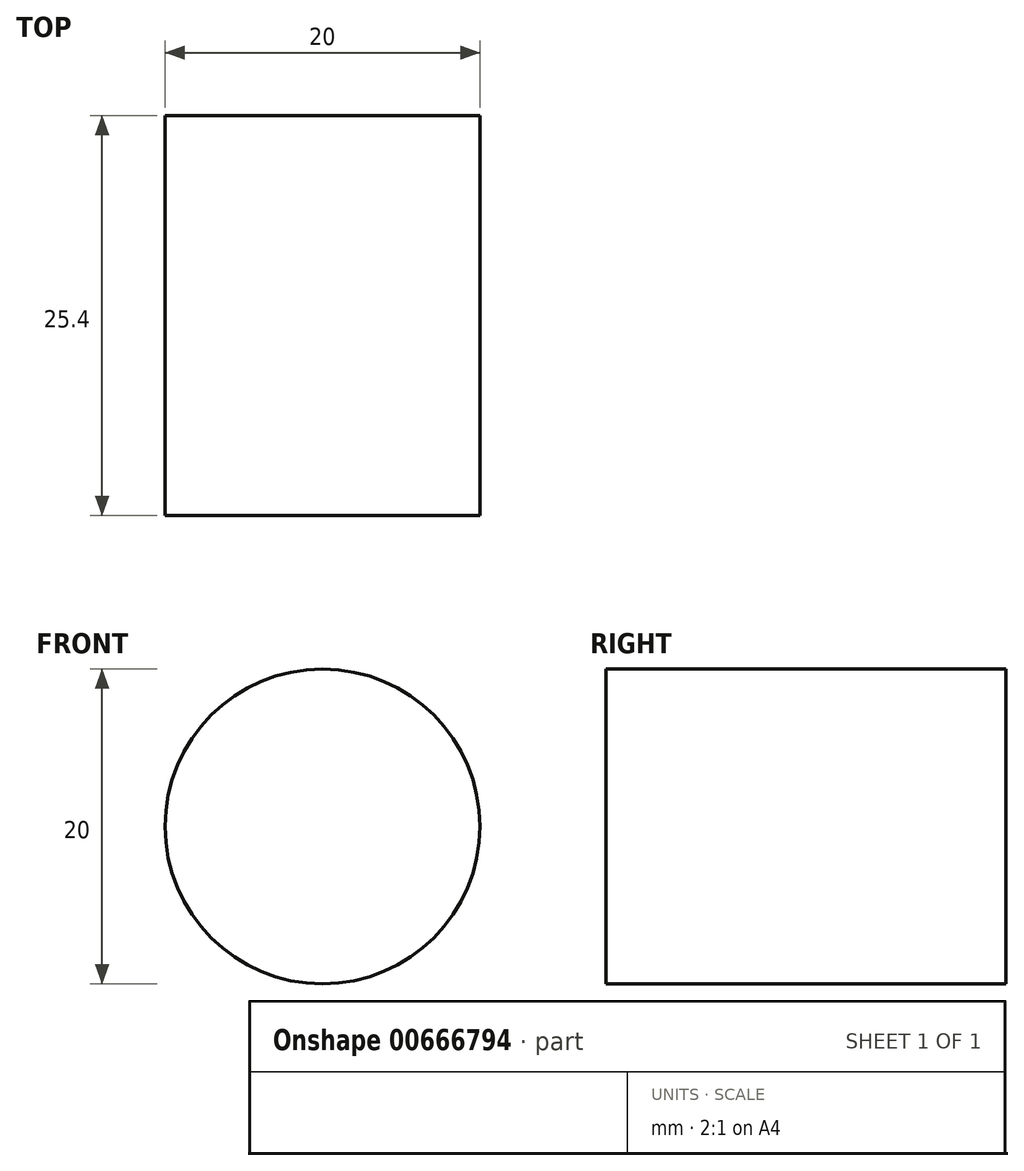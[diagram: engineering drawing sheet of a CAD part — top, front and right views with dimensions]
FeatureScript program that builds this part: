
annotation { "Feature Type Name" : "Feature", "Feature Type Description" : "" }
export const myFeature = defineFeature(function(context is Context, id is Id, definition is map)
    precondition{}
    {
        {
            var Q0;
            Q0=qCreatedBy(makeId("Front.planeOp"),FACE);
            var sketch = newSketch(context, id + "F0", { "sketchPlane" : qUnion([Q0])});
            skCircle(sketch, "E0", {"center": v(-1.71, 0) * mm, "radius": 10 * mm});
            skCircle(sketch, "E1", {"center": v(10.49, 5) * mm, "radius": 2.5 * mm});
            skSolve(sketch);
        }
        {
            var Q0;
            Q0=makeQuery(id+"F0.imprint","IMPRINT",FACE,{"disambiguationData":[TD([[makeQuery(id+"F0.imprint","IMPRINT",EDGE,{"derivedFrom":sQuery(id+"F0.wireOp",EDGE,"E0")}),1.0]])]});
            extrude(context, id + "F1", {"entities" : qUnion([Q0]), "depth" : 25.4 * mm, "offsetDistance" : 25.4 * mm});
        }
    });
